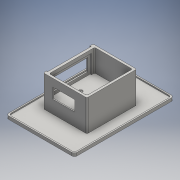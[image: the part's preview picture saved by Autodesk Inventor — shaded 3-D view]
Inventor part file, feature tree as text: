
AUTODESK INVENTOR PART (.ipt)
format: ipt  version: 2016 (Build 200138000, 138)  size: 257,024 bytes
history: native  units: mm
features: extrude x10, sketch x10
ambient origin geometry x8: Origin, YZ Plane, XZ Plane, XY Plane, X Axis, Y Axis, Z Axis, Center Point
bodies: Solid1 (feature_tree)
feature tree (20):
  extrude  "xyAttach"  Depth=159.5mm
  extrude  "spillExtrusion"  Depth=79.75mm
  extrude  "chamberWallExtrusion"  Depth=3.0mm TaperAngle=0.0deg
  extrude  "chamberInteriorExtrusion"  Depth=4.0mm
  extrude  "rectCoverSlipMountExtrusion"  Depth=2.0mm
  extrude  "rectCoverSlipWindow"  Depth=2.0mm
  extrude  "illObjExtrusion"  Depth=70.0mm
  extrude  "viewingWindowCoverslipMount"  Depth=80.0mm
  extrude  "viewingWindowExt"  Depth=2.0mm
  extrude  "sampleMountExt"  Depth=2.0mm
  sketch  "Sketch1"  dims[d0=109.5mm d1=159.5mm]
  sketch  "Sketch2"  dims[d2=54.75mm d3=79.75mm]
  sketch  "Sketch3"  dims[d4=4.0mm d5=3.0mm d6=0.0mm]
  sketch  "Sketch4"  dims[d7=4.0mm d8=4.0mm]
  sketch  "Sketch5"  dims[d9=2.0mm d10=2.0mm]
  sketch  "Sketch6"  dims[d11=2.0mm d12=2.0mm]
  sketch  "Sketch7"  dims[d13=2.0mm d14=0.0mm d15=70.0mm]
  sketch  "Sketch8"  dims[d16=35.0mm d17=80.0mm]
  sketch  "Sketch9"  dims[d18=40.0mm d19=2.0mm]
  sketch  "Sketch10"  dims[d20=50.0mm d21=0.0mm d22=2.0mm d23=3.5mm d24=3.5mm d25=3.5mm d26=6.0mm d27=35.5mm d28=0.0mm d29=62.5mm d30=30.0mm d31=31.25mm d32=42.5mm d33=2.0mm d34=0.0mm d35=55.0mm d36=20.0mm d37=37.5mm d38=27.5mm d39=2.0mm d40=0.0mm d41=70.0mm d42=35.0mm d43=2.0mm d44=0.0mm d46=45.0mm d47=25.0mm d48=40.0mm d50=2.0mm d51=0.0mm d52=35.0mm d53=17.0mm d55=36.0mm d56=2.0mm d57=0.0mm d58=5.65mm d59=5.65mm d60=5.65mm d61=5.65mm d62=5.65mm d63=15.0mm d64=15.0mm d65=15.0mm d66=15.0mm d67=2.0mm d68=0.0mm d69=4.5mm d71=5.0mm]
